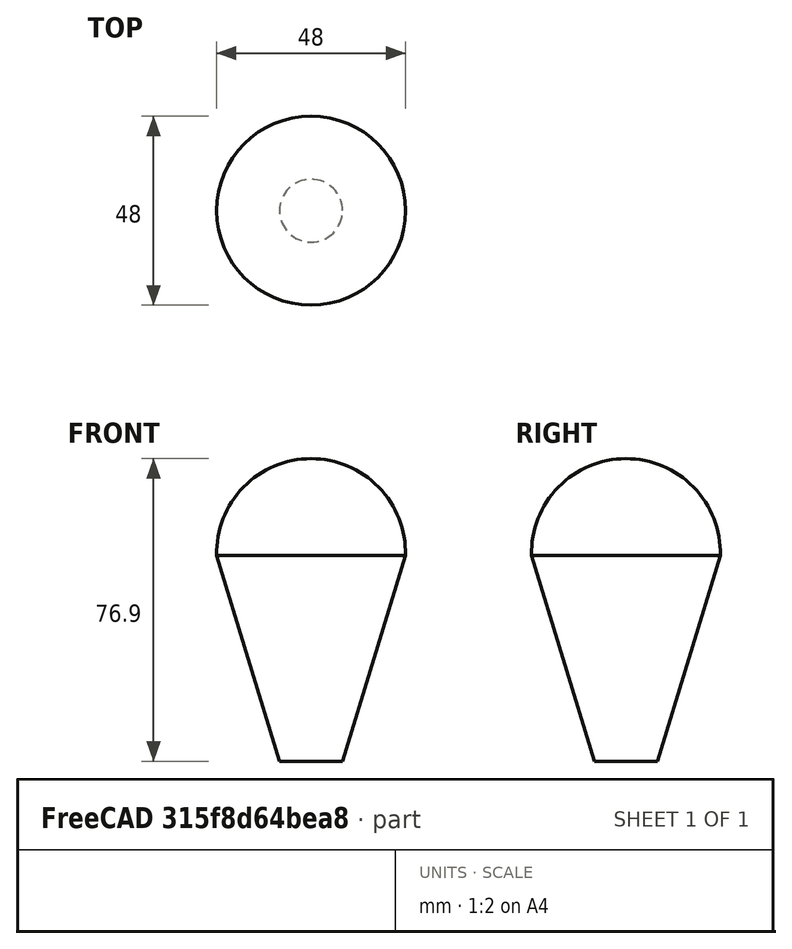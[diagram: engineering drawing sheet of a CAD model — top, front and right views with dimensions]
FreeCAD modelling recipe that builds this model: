
FCSTD DOCUMENT  (FreeCAD 0.21R32552 (Git))
Label: orientation planes
License: All rights reserved
LicenseURL: http://en.wikipedia.org/wiki/All_rights_reserved
objects: TechDraw::DrawViewDimension×5, Sketcher::SketchObject×1, PartDesign::Revolution×1, PartDesign::Body×1, TechDraw::DrawSVGTemplate×1, TechDraw::DrawProjGroupItem×1, TechDraw::DrawProjGroup×1, TechDraw::DrawViewAnnotation×1, TechDraw::DrawViewBalloon×1, TechDraw::DrawPage×1
note: 12 computed .brp shape members not serialized (recipe doc carries the construction recipe); baked Part::Feature solids carry a one-line shape summary decoded from their .brp

FEATURE [Sketcher::SketchObject] Sketch
  FullyConstrained = true
  MapMode = 5
  Placement = pos=(0,0,0) rot=(1,0,0;1.5708rad)
  Support = -> [XZ_Plane]
  sketch-geometry (5):
    g0: LineSegment StartX=7.3e-15 StartY=0 StartZ=0 EndX=8 EndY=0 EndZ=0
    g1: LineSegment StartX=8 StartY=0 StartZ=0 EndX=23.9929 EndY=52.3103 EndZ=0
    g2: ArcOfCircle CenterX=0 CenterY=52.896 CenterZ=0 NormalX=0 NormalY=0 NormalZ=1 AngleXU=0 Radius=24 StartAngle=6.25878 EndAngle=7.85398
    g3: LineSegment StartX=7.3e-15 StartY=0 StartZ=0 EndX=7.3e-15 EndY=76.896 EndZ=0
    g4: LineSegment StartX=15 StartY=22.896 StartZ=0 EndX=0 EndY=22.896 EndZ=0
  constraints (16):
    c: Coincident(g0,g-1)
    c: PointOnObject(g0,g-1)
    c: Coincident(g1,g0)
    c: PointOnObject(g2,g-2)
    c: Coincident(g3,g0)
    c: Vertical(g3)
    c: Coincident(g2,g3)
    c: Coincident(g2,g1)
    c: Angle(g1,g3) = 0.296706
    c: Diameter(g2) = 48
    c: PointOnObject(g4,g1)
    c: PointOnObject(g4,g3)
    c: Horizontal(g4)
    c: DistanceX(g0,g0) = 8
    c: DistanceY(g4,g2) = 30
    c: DistanceX(g4,g4) = 15
FEATURE [PartDesign::Revolution] Revolution
  Angle = 360
  Axis = (0,2e-16,1)
  Base = (0,0,0)
  Placement = pos=(0,0,0) rot=(1,0,0;1.5708rad)
  Profile = -> Sketch
  ReferenceAxis = -> Sketch [V_Axis]
  Reversed = true
FEATURE [PartDesign::Body] Body
  Group = -> [Sketch,Revolution]
  Origin = -> Origin
  Tip = -> Revolution
FEATURE [TechDraw::DrawSVGTemplate] Template
  Height = 297
  Orientation = 1
  Template = <path> 0.21/data/Mod/TechDraw/Templates/A3_Landscape_FR_m52.svg
  Width = 420
FEATURE [TechDraw::DrawProjGroupItem] ProjItem  label="Figure 84"
  CoarseView = false
  Direction = (0,-1,0)
  Focus = 100
  HardHidden = false
  IsoCount = 0
  IsoHidden = false
  IsoVisible = false
  LockPosition = true
  Perspective = false
  Rotation = 0
  RotationVector = (1,0,0)
  ScaleType = 2
  SeamHidden = false
  SeamVisible = true
  SmoothHidden = false
  SmoothVisible = true
  Source = -> [Body]
  Type = 0
  X = 0
  XDirection = (1,0,0)
  Y = 0
FEATURE [TechDraw::DrawProjGroup] ProjGroup
  Anchor = -> ProjItem
  AutoDistribute = true
  LockPosition = false
  ProjectionType = 0
  Rotation = 0
  ScaleType = 0
  Source = -> [Body]
  Views = -> [ProjItem]
  X = 210
  Y = 148.5
  spacingX = 15
  spacingY = 15
FEATURE [TechDraw::DrawViewDimension] Dimension
  AngleOverride = false
  Arbitrary = true
  ArbitraryTolerances = false
  EqualTolerance = true
  ExtensionAngle = 0
  FormatSpecOverTolerance = %+.3f
  FormatSpecUnderTolerance = %+.3f
  Inverted = false
  LineAngle = 0
  LockPosition = false
  MeasureType = 1
  OverTolerance = 0
  References2D = -> [ProjItem]
  Rotation = 0
  ScaleType = 0
  TheoreticalExact = false
  Type = 5
  UnderTolerance = 0
  X = -45.1646
  Y = 40.6731
FEATURE [TechDraw::DrawViewAnnotation] Annotation
  Font = Iso-Gps
  LineSpace = 96
  LockPosition = false
  MaxWidth = -1
  Rotation = 0
  ScaleType = 0
  Text = ǱǧȓȒȕǧǸɕǾǯɕȀ\n\n | ǱǧȄȓȒȓȕǧǸɕǾǮɕȀ
  TextSize = 5
  TextStyle = 0
  X = 122.025
  Y = 187.426
FEATURE [TechDraw::DrawViewDimension] Dimension001
  AngleOverride = false
  Arbitrary = false
  ArbitraryTolerances = false
  EqualTolerance = true
  ExtensionAngle = 0
  FormatSpec = %.0f
  FormatSpecOverTolerance = %+.3f
  FormatSpecUnderTolerance = %+.3f
  Inverted = false
  LineAngle = 0
  LockPosition = false
  MeasureType = 1
  OverTolerance = 0
  References2D = -> [ProjItem]
  Rotation = 0
  ScaleType = 0
  TheoreticalExact = true
  Type = 6
  UnderTolerance = 0
  X = -0.221376
  Y = -13.6604
FEATURE [TechDraw::DrawViewBalloon] Balloon
  BubbleShape = 5
  EndType = 6
  EndTypeScale = 1
  KinkLength = 0.0001
  LockPosition = false
  OriginX = -15.9964
  OriginY = -12.2929
  Rotation = 0
  ScaleType = 0
  ShapeScale = 1
  SourceView = -> ProjItem
  Text = D
  TextWrapLen = -1
  X = -29.7239
  Y = -12.2416
FEATURE [TechDraw::DrawViewDimension] Dimension003
  AngleOverride = false
  Arbitrary = false
  ArbitraryTolerances = false
  EqualTolerance = true
  ExtensionAngle = 0
  FormatSpec = ⌀%.3f
  FormatSpecOverTolerance = %+.3f
  FormatSpecUnderTolerance = %+.3f
  Inverted = false
  LineAngle = 0
  LockPosition = false
  MeasureType = 1
  OverTolerance = 0
  References2D = -> [ProjItem]
  Rotation = 0
  ScaleType = 0
  TheoreticalExact = true
  Type = 1
  UnderTolerance = 0
  X = -0.125696
  Y = 7.43266
FEATURE [TechDraw::DrawViewDimension] Dimension004
  AngleOverride = false
  Arbitrary = false
  ArbitraryTolerances = false
  EqualTolerance = true
  ExtensionAngle = 0
  FormatSpec = %.3f
  FormatSpecOverTolerance = %+.3f
  FormatSpecUnderTolerance = %+.3f
  Inverted = false
  LineAngle = 0
  LockPosition = false
  MeasureType = 1
  OverTolerance = 0
  References2D = -> [ProjItem]
  Rotation = 0
  ScaleType = 0
  TheoreticalExact = true
  Type = 2
  UnderTolerance = 0
  X = -40.9184
  Y = 10.3677
FEATURE [TechDraw::DrawViewDimension] Dimension005
  AngleOverride = false
  Arbitrary = false
  ArbitraryTolerances = false
  EqualTolerance = true
  ExtensionAngle = 0
  FormatSpec = R%.0f
  FormatSpecOverTolerance = %+.3f
  FormatSpecUnderTolerance = %+.3f
  Inverted = false
  LineAngle = 0
  LockPosition = false
  MeasureType = 1
  OverTolerance = 0
  References2D = -> [ProjItem]
  Rotation = 0
  ScaleType = 0
  TheoreticalExact = false
  Type = 4
  UnderTolerance = 0
  X = 41.1721
  Y = 53.6486
FEATURE [TechDraw::DrawPage] Page
  KeepUpdated = true
  NextBalloonIndex = 2
  ProjectionType = 0
  Template = -> Template
  Views = -> [ProjGroup,Dimension,Annotation,Dimension001,Balloon,Dimension003,Dimension004,Dimension005]
note: 1 file-system path scrubbed to <path> (originals preserved in the JSON sidecar)
